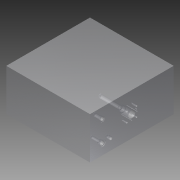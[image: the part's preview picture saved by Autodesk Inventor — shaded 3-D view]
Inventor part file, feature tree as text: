
AUTODESK INVENTOR PART (.ipt)
format: ipt  version: 2014 (Build 180170000, 170)  size: 433,152 bytes
history: native  units: mm
features: other x48, extrude x39, sketch x39
ambient origin geometry x8: Origin, YZ Plane, XZ Plane, XY Plane, X Axis, Y Axis, Z Axis, Center Point
bodies: 实体1 (feature_tree)
feature tree (126):
  extrude  "拉伸1"  Depth=30.0mm
  other  "UCS1"
  other  "UCS2"
  other  "UCS3"
  other  "UCS4"
  other  "UCS5"
  other  "UCS6"
  extrude  "拉伸3"  Depth=60.0mm
  extrude  "拉伸5"  Depth=2.0mm
  extrude  "拉伸6"  Depth=2.4mm
  extrude  "拉伸7"  Depth=14.5mm TaperAngle=0.0deg
  extrude  "拉伸8"  Depth=16.5mm TaperAngle=0.0deg
  extrude  "拉伸9"  Depth=11.0mm
  extrude  "拉伸10"  Depth=50.8mm
  extrude  "拉伸11"  Depth=150.0mm
  extrude  "拉伸12"  Depth=1.5mm TaperAngle=0.0deg
  extrude  "拉伸13"  Depth=12.5mm TaperAngle=0.0deg
  extrude  "拉伸14"  Depth=16.0mm TaperAngle=0.0deg
  extrude  "拉伸15"  Depth=14.0mm
  extrude  "拉伸16"  Depth=38.1mm
  extrude  "拉伸17"  Depth=14.0mm
  extrude  "拉伸18"  Depth=14.5mm TaperAngle=0.0deg
  extrude  "拉伸20"  Depth=12.7mm
  extrude  "拉伸21"  Depth=20.0mm
  extrude  "拉伸22"  Depth=100.0mm
  extrude  "拉伸23"  Depth=200.0mm
  extrude  "拉伸24"  Depth=10.0mm
  extrude  "拉伸25"  Depth=43.0mm TaperAngle=0.0deg
  extrude  "拉伸26"  Depth=13.0mm
  extrude  "拉伸28"  Depth=56.0mm TaperAngle=0.0deg
  extrude  "拉伸29"  Depth=16.0mm TaperAngle=0.0deg
  extrude  "拉伸30"  Depth=6.75mm
  extrude  "拉伸31"  Depth=23.0mm
  extrude  "拉伸32"  Depth=23.0mm
  extrude  "拉伸33"  Depth=23.0mm
  extrude  "拉伸34"  Depth=23.0mm
  extrude  "拉伸35"  Depth=24.0mm
  extrude  "拉伸36"  Depth=24.0mm
  extrude  "拉伸37"  Depth=8.0mm
  extrude  "拉伸38"  Depth=16.0mm TaperAngle=0.0deg
  extrude  "拉伸39"  Depth=4.0mm
  extrude  "拉伸40"  Depth=4.0mm
  extrude  "拉伸41"  TaperAngle=0.0deg  [1 undecoded]
  extrude  "拉伸42"  TaperAngle=0.0deg  [1 undecoded]
  extrude  "拉伸43"  Depth=8.0mm
  sketch  "草图1"  dims[d0=200.0mm d1=0.0mm]
  sketch  "草图2"  dims[d2=0.0mm d3=0.0mm d4=0.0mm d5=0.0mm d6=0.0mm d7=0.0mm]
  sketch  "草图4"  dims[d8=0.0mm d9=0.0mm d10=0.0mm d11=0.0mm d12=0.0mm d13=0.0mm]
  sketch  "草图5"  dims[d14=0.0mm d15=0.0mm d16=0.0mm d17=0.0mm d18=0.0mm d19=0.0mm]
  sketch  "草图6"  dims[d20=0.0mm d21=0.0mm d22=0.0mm d23=0.0mm d24=0.0mm d25=0.0mm]
  sketch  "草图8"  dims[d26=0.0mm d27=0.0mm d28=0.0mm d29=0.0mm d30=0.0mm d31=0.0mm]
  sketch  "草图9"  dims[d32=0.0mm d33=0.0mm d34=0.0mm d35=0.0mm d36=0.0mm d37=0.0mm d38=30.0mm]
  sketch  "草图10"  dims[d39=50.0mm d40=60.0mm]
  sketch  "草图11"  dims[d43=2.0mm d44=0.0mm d47=19.8mm]
  sketch  "草图15"  dims[d48=2.4mm d49=-2.617994mm d50=2.4mm d51=-7.853982mm]
  sketch  "草图16"  dims[d52=18.0mm d53=14.5mm d54=0.0mm]
  sketch  "草图17"  dims[d55=16.5mm d56=17.0mm d57=0.0mm]
  sketch  "草图18"  dims[d58=17.0mm d59=-10.471976mm d60=11.0mm]
  sketch  "草图19"  dims[d61=50.8mm d62=0.0mm d63=50.8mm d64=-10.297443mm]
  sketch  "草图20"  dims[d74=60.0mm d75=150.0mm]
  sketch  "草图21"  dims[d76=24.5mm d77=1.5mm d78=0.0mm]
  sketch  "草图23"  dims[d79=16.7mm d80=12.5mm d81=0.0mm]
  sketch  "草图24"  dims[d82=15.25mm d83=16.0mm d84=0.0mm]
  sketch  "草图25"  dims[d85=16.0mm d86=-10.297443mm d87=14.0mm]
  sketch  "草图27"  dims[d88=38.1mm d89=0.0mm d90=38.1mm d91=-10.297443mm]
  sketch  "草图28"  dims[d92=14.0mm d93=50.0mm]
  sketch  "草图29"  dims[d94=100.0mm d95=14.5mm d96=0.0mm]
  sketch  "草图31"  dims[d100=20.0mm d101=-10.471976mm d102=12.7mm]
  sketch  "草图32"  dims[d103=20.0mm d104=0.0mm d105=20.0mm d106=-10.297443mm]
  sketch  "草图33"  dims[d110=33.7mm d111=100.0mm]
  sketch  "草图34"  dims[d112=200.0mm d113=65.0mm]
  sketch  "草图35"  dims[d114=65.0mm d115=10.0mm d116=-2.617994mm]
  sketch  "草图36"  dims[d117=32.0mm d118=43.0mm d119=0.0mm]
  sketch  "草图37"  dims[d120=26.07mm d121=13.0mm d122=-2.617994mm]
  sketch  "草图38"  dims[d124=25.0mm d125=56.0mm d126=0.0mm]
  sketch  "草图39"  dims[d127=16.0mm d130=152.4mm d131=0.0mm]
  sketch  "草图40"  dims[d132=152.4mm d133=-10.297443mm d134=6.75mm]
  sketch  "草图41"  dims[d135=23.0mm d136=23.0mm]
  sketch  "草图42"  dims[d137=23.0mm d138=23.0mm]
  sketch  "草图43"  dims[d139=23.0mm d140=23.0mm]
  sketch  "草图44"  dims[d141=23.0mm d142=23.0mm]
  sketch  "草图45"  dims[d143=24.0mm d144=0.0mm d145=24.0mm d146=-10.297443mm]
  sketch  "草图46"  dims[d147=24.0mm d148=-10.297443mm d149=24.0mm d150=-10.297443mm]
  sketch  "草图47"  dims[d151=24.0mm d152=-10.297443mm d153=8.0mm d154=16.0mm d155=0.0mm d156=4.0mm d157=4.0mm d160=0.0mm d161=0.0mm d162=25.0mm d163=25.000195mm d164=25.4mm d165=0.0mm d166=25.4mm d167=-10.297443mm d168=25.4mm d169=-10.297443mm d170=4.0mm d171=4.0mm d172=25.0mm d173=0.0mm d174=25.0mm d175=0.0mm d176=25.4mm d177=0.0mm d178=25.4mm d179=-10.297443mm d180=25.4mm d181=-10.297443mm d182=4.0mm d183=23.0mm d184=10.5mm d185=8.0mm d186=0.0mm d187=8.0mm d188=-10.297443mm]
  other  "UCS1: YZ 平面"
  other  "UCS1: XZ 平面"
  other  "UCS1: XY 平面"
  other  "UCS1: X 轴"
  other  "UCS1: Y 轴"
  other  "UCS1: Z 轴"
  other  "UCS1: 原点"
  other  "UCS2: YZ 平面"
  other  "UCS2: XZ 平面"
  other  "UCS2: XY 平面"
  other  "UCS2: X 轴"
  other  "UCS2: Y 轴"
  other  "UCS2: Z 轴"
  other  "UCS2: 原点"
  other  "UCS3: YZ 平面"
  other  "UCS3: XZ 平面"
  other  "UCS3: XY 平面"
  other  "UCS3: X 轴"
  other  "UCS3: Y 轴"
  other  "UCS3: Z 轴"
  other  "UCS3: 原点"
  other  "UCS4: YZ 平面"
  other  "UCS4: XZ 平面"
  other  "UCS4: XY 平面"
  other  "UCS4: X 轴"
  other  "UCS4: Y 轴"
  other  "UCS4: Z 轴"
  other  "UCS4: 原点"
  other  "UCS5: YZ 平面"
  other  "UCS5: XZ 平面"
  other  "UCS5: XY 平面"
  other  "UCS5: X 轴"
  other  "UCS5: Y 轴"
  other  "UCS5: Z 轴"
  other  "UCS5: 原点"
  other  "UCS6: YZ 平面"
  other  "UCS6: XZ 平面"
  other  "UCS6: XY 平面"
  other  "UCS6: X 轴"
  other  "UCS6: Y 轴"
  other  "UCS6: Z 轴"
  other  "UCS6: 原点"
note: 2 required parameter values undecoded (feature->parameter linkage not recoverable at this tier; creation-order binding heuristic only, values carry confidence <= 0.55)
